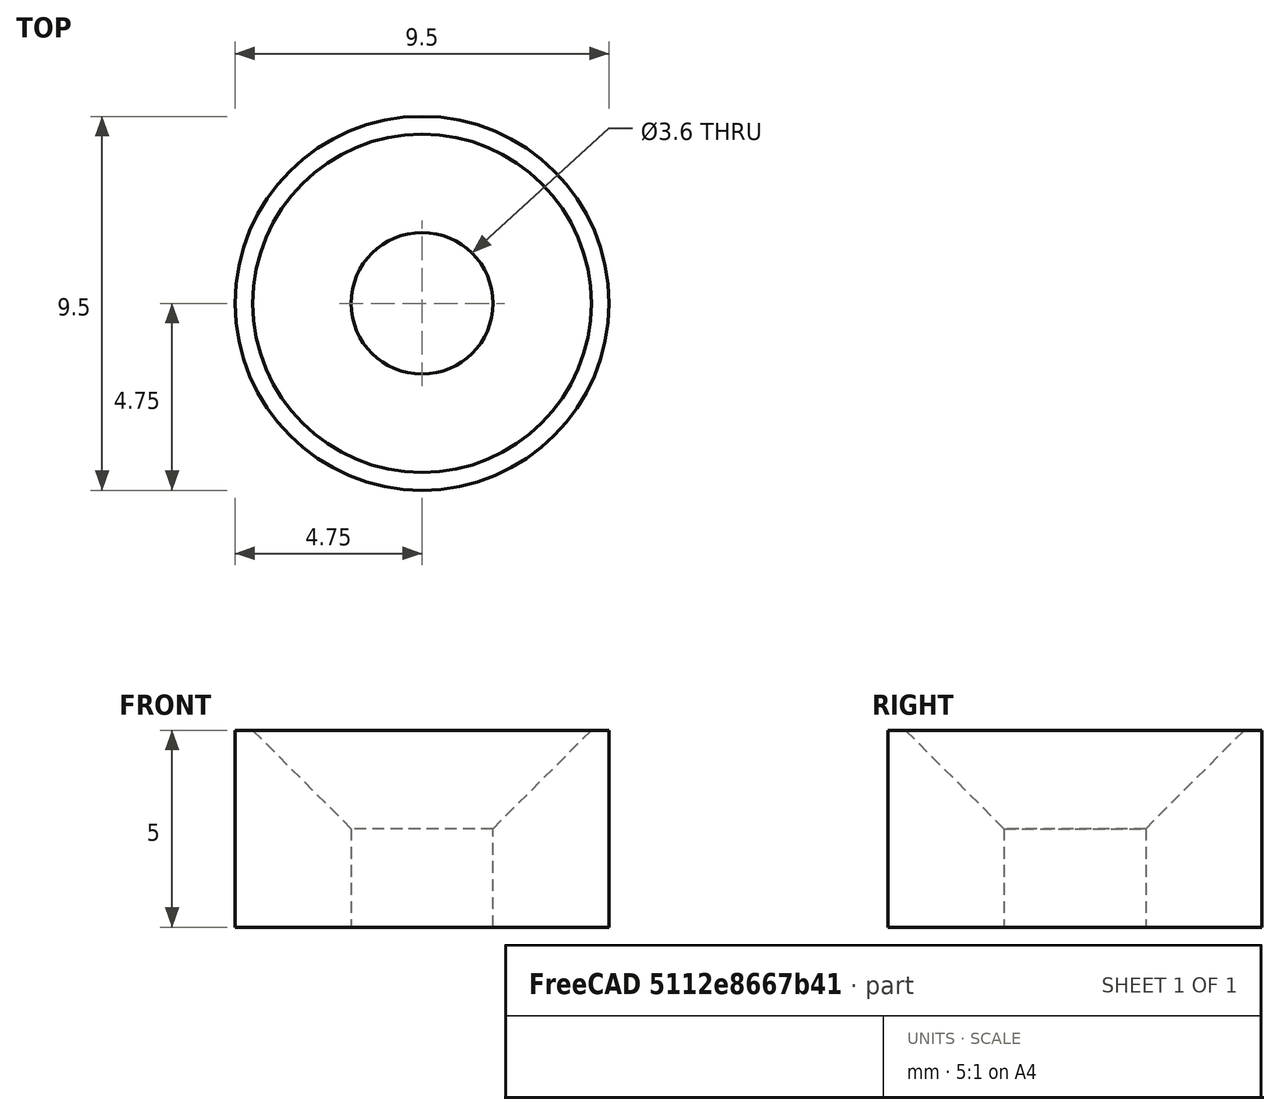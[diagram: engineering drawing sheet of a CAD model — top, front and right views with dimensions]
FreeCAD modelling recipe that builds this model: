
FCSTD DOCUMENT  (FreeCAD 0.21R33668 +7 (Git))
Label: leg-pivot2
License: All rights reserved
LicenseURL: http://en.wikipedia.org/wiki/All_rights_reserved
objects: Sketcher::SketchObject×1, PartDesign::Pad×1, PartDesign::Chamfer×1, PartDesign::Body×1
note: 6 computed .brp shape members not serialized (recipe doc carries the construction recipe); baked Part::Feature solids carry a one-line shape summary decoded from their .brp

FEATURE [Sketcher::SketchObject] Sketch
  FullyConstrained = true
  MapMode = 5
  Support = -> [XY_Plane]
  sketch-geometry (2):
    g0: Circle CenterX=0 CenterY=0 CenterZ=0 NormalX=0 NormalY=0 NormalZ=1 AngleXU=0 Radius=4.75
    g1: Circle CenterX=0 CenterY=0 CenterZ=0 NormalX=0 NormalY=0 NormalZ=1 AngleXU=0 Radius=1.8
  constraints (4):
    c: Coincident(g0,g-1)
    c: Coincident(g1,g0)
    c: Diameter(g0) = 9.5
    c: Diameter(g1) = 3.6
FEATURE [PartDesign::Pad] Pad
  Direction = (0,0,1)
  Length = 5
  Length2 = 10
  Profile = -> Sketch
  ReferenceAxis = -> Sketch [N_Axis]
  Type = 0
FEATURE [PartDesign::Chamfer] Chamfer
  Angle = 45
  Base = -> Pad [Edge6]
  BaseFeature = -> Pad
  ChamferType = 0
  FlipDirection = false
  Size = 2.5
  Size2 = 1
  SupportTransform = false
  UseAllEdges = false
FEATURE [PartDesign::Body] Body
  Group = -> [Sketch,Pad,Chamfer]
  Origin = -> Origin
  Tip = -> Chamfer
